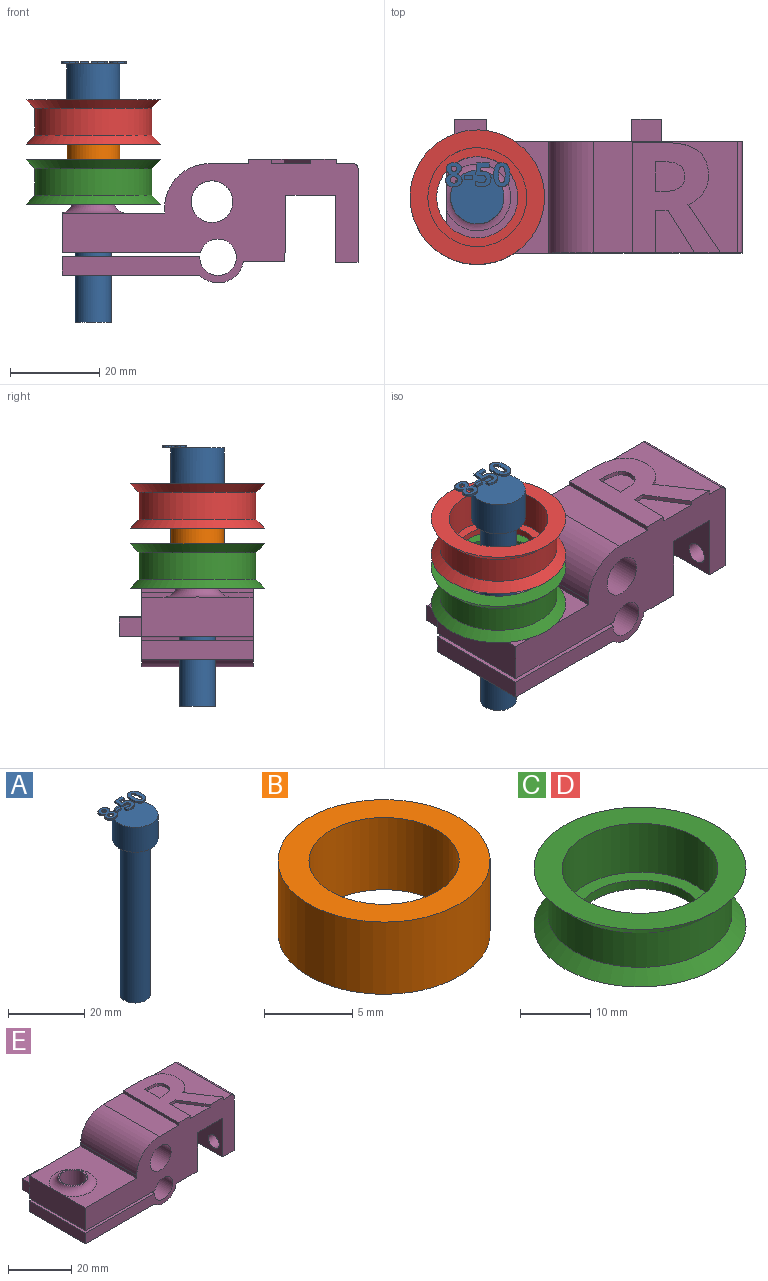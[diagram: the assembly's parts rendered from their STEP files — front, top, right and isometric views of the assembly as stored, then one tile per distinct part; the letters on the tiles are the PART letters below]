
ASSEMBLY  parts=5 mates=4
PART A: 86 faces, bbox 14.5x13.7x58.5 mm
  f0: plane 12x12mm, normal (0,0,1), area 99.4mm2, adj f5,f22,f23,f24,f25,f26,f40,f41
  f1: plane 1x0.26mm, normal (0,0,1), area 0.1mm2, adj f5,f46,f47,f48,f49
  f2: plane 0.85x0.68mm, normal (0,0,1), area 0.2mm2, adj f5,f29,f30,f31
  f3: cylinder r=4mm len=50mm, axis (0,0,-1), area 1256.6mm2, adj f4,f6
  f4: plane 8x8mm, normal (0,0,-1), area 50.3mm2, adj f3
  f5: cylinder r=6mm len=12mm, axis (0,0,-1), area 301.6mm2, adj f0,f1,f2,f6,f39,f45,f67,f85
  f6: plane 12x12mm, normal (0,0,-1), area 62.8mm2, adj f3,f5
  f7: extruded ~0.5x0.46mm, area 0.2mm2, adj f8,f37,f38,f39
  f8: extruded ~0.5x0.46mm, area 0.2mm2, adj f7,f9,f38,f39
  f9: extruded ~0.5x0.39mm, area 0.2mm2, adj f8,f10,f38,f39
  f10: extruded ~0.5x0.4mm, area 0.2mm2, adj f9,f11,f38,f39
  f11: extruded ~0.5x0.49mm, area 0.3mm2, adj f10,f12,f38,f39
  f12: extruded ~0.5x0.5mm, area 0.3mm2, adj f11,f13,f38,f39
  f13: extruded ~0.5x0.39mm, area 0.2mm2, adj f12,f37,f38,f39
  f14: extruded ~1.22x0.5mm, area 0.6mm2, adj f15,f35,f38,f39
  f15: extruded ~1.22x0.5mm, area 0.6mm2, adj f14,f16,f38,f39
  f16: extruded ~0.91x0.5mm, area 0.5mm2, adj f15,f17,f38,f39
  f17: extruded ~0.71x0.5mm, area 0.4mm2, adj f16,f18,f38,f39
  f18: extruded ~0.65x0.61mm, area 0.4mm2, adj f17,f19,f38,f39
  f19: extruded ~0.77x0.62mm, area 0.5mm2, adj f18,f20,f38,f39
  f20: extruded ~0.8x0.5mm, area 0.4mm2, adj f19,f21,f38,f39
  f21: extruded ~1.04x0.5mm, area 0.6mm2, adj f20,f22,f38,f39
  f22: extruded ~1.36x0.5mm, area 0.7mm2, adj f0,f21,f23,f38,f39
  f23: extruded ~1.33x0.5mm, area 0.7mm2, adj f0,f22,f24,f38
  f24: extruded ~1.04x0.51mm, area 0.6mm2, adj f0,f23,f25,f38
  f25: extruded ~0.75x0.5mm, area 0.4mm2, adj f0,f24,f26,f38
  f26: extruded ~0.85x0.66mm, area 0.5mm2, adj f0,f25,f27,f38,f39
  f27: extruded ~0.72x0.56mm, area 0.5mm2, adj f26,f28,f38,f39
  f28: extruded ~0.72x0.5mm, area 0.4mm2, adj f27,f35,f38,f39
  f29: extruded ~0.5x0.45mm, area 0.3mm2, adj f2,f30,f36,f38,f39
  f30: extruded ~0.5x0.47mm, area 0.3mm2, adj f2,f29,f31,f38
  f31: extruded ~0.62x0.5mm, area 0.3mm2, adj f2,f30,f32,f38,f39
  f32: extruded ~0.59x0.5mm, area 0.3mm2, adj f31,f33,f38,f39
  f33: extruded ~0.5x0.48mm, area 0.3mm2, adj f32,f34,f38,f39
  f34: extruded ~0.89x0.77mm, area 0.6mm2, adj f33,f36,f38,f39
  f35: extruded ~0.93x0.5mm, area 0.5mm2, adj f14,f28,f38,f39
  f36: extruded ~0.66x0.5mm, area 0.4mm2, adj f29,f34,f38,f39
  f37: extruded ~0.5x0.39mm, area 0.2mm2, adj f7,f13,f38,f39
  f38: plane 5.4x3.69mm, normal (0,0,1), area 12.7mm2, adj f7,f8,f9,f10,f11,f12,f13,f14
  f39: plane 5.4x3.53mm, normal (0,0,-1), area 10.2mm2, adj f5,f7,f8,f9,f10,f11,f12,f13
  f40: plane 0.9x0.5mm, normal (-1,0,0), area 0.4mm2, adj f0,f41,f43,f44
  f41: plane 1.93x0.5mm, normal (0,-1,0), area 1mm2, adj f0,f40,f42,f44
  f42: plane 0.9x0.5mm, normal (1,0,0), area 0.4mm2, adj f0,f41,f43,f44
  f43: plane 1.93x0.5mm, normal (0,1,0), area 1mm2, adj f0,f40,f42,f44
  f44: plane 1.93x0.9mm, normal (0,0,1), area 1.7mm2, adj f40,f41,f42,f43
  f45: plane 0.76x0.31mm, normal (0,0,-1), area 0mm2, adj f5,f46
  f46: extruded ~1.21x0.5mm, area 0.7mm2, adj f0,f1,f45,f47,f65,f66
  f47: extruded ~0.54x0.5mm, area 0.3mm2, adj f1,f46,f48,f66
  f48: plane 0.5x0.13mm, normal (-0.2,0.98,0), area 0.1mm2, adj f1,f47,f49,f66
  f49: plane 1.03x0.5mm, normal (1,-0.09,0), area 0.5mm2, adj f1,f48,f50,f66,f67
  f50: plane 1.88x0.5mm, normal (0,-1,0), area 0.9mm2, adj f49,f51,f66,f67
  f51: plane 0.94x0.5mm, normal (1,0,0), area 0.5mm2, adj f50,f52,f66,f67
  f52: plane 2.85x0.5mm, normal (0,1,0), area 1.4mm2, adj f51,f53,f66,f67
  f53: plane 2.68x0.5mm, normal (-1,0.07,0), area 1.3mm2, adj f0,f52,f54,f66,f67
  f54: plane 0.5x0.44mm, normal (-0.47,-0.88,0), area 0.3mm2, adj f0,f53,f55,f66
  f55: extruded ~0.5x0.37mm, area 0.2mm2, adj f0,f54,f56,f66
  f56: extruded ~0.5x0.42mm, area 0.2mm2, adj f0,f55,f57,f66
  f57: extruded ~1.05x0.8mm, area 0.8mm2, adj f0,f56,f58,f66
  f58: extruded ~1.02x0.83mm, area 0.8mm2, adj f0,f57,f59,f66
  f59: extruded ~0.72x0.5mm, area 0.4mm2, adj f0,f58,f60,f66
  f60: extruded ~0.66x0.5mm, area 0.4mm2, adj f0,f59,f61,f66
  f61: plane 0.96x0.5mm, normal (-1,0,0), area 0.5mm2, adj f0,f60,f62,f66
  f62: extruded ~1.42x0.5mm, area 0.7mm2, adj f0,f61,f63,f66
  f63: extruded ~1.55x0.5mm, area 0.8mm2, adj f0,f62,f64,f66
  f64: extruded ~1.36x0.54mm, area 0.8mm2, adj f0,f63,f65,f66
  f65: extruded ~1.17x0.5mm, area 0.6mm2, adj f0,f46,f64,f66
  f66: plane 5.33x3.51mm, normal (0,0,1), area 10.9mm2, adj f46,f47,f48,f49,f50,f51,f52,f53
  f67: plane 2.97x1.71mm, normal (0,0,-1), area 3.5mm2, adj f5,f49,f50,f51,f52,f53
  f68: extruded ~1.39x0.5mm, area 0.7mm2, adj f69,f83,f84,f85
  f69: extruded ~1.39x0.5mm, area 0.7mm2, adj f68,f70,f84,f85
  f70: extruded ~0.56x0.5mm, area 0.4mm2, adj f69,f71,f84,f85
  f71: extruded ~0.56x0.5mm, area 0.4mm2, adj f70,f72,f84,f85
  f72: extruded ~1.39x0.5mm, area 0.7mm2, adj f71,f73,f84,f85
  f73: extruded ~1.38x0.5mm, area 0.7mm2, adj f72,f74,f84,f85
  f74: extruded ~0.56x0.5mm, area 0.4mm2, adj f73,f83,f84,f85
  f75: extruded ~2.04x0.5mm, area 1.1mm2, adj f76,f82,f84,f85
  f76: extruded ~2.02x0.5mm, area 1.1mm2, adj f75,f77,f84,f85
  f77: extruded ~1.38x0.69mm, area 0.8mm2, adj f76,f78,f84,f85
  f78: extruded ~1.38x0.66mm, area 0.8mm2, adj f77,f79,f84,f85
  f79: extruded ~2.05x0.5mm, area 1.1mm2, adj f78,f80,f84,f85
  f80: extruded ~2.02x0.5mm, area 1mm2, adj f0,f79,f81,f84,f85
  f81: extruded ~1.37x0.68mm, area 0.8mm2, adj f0,f80,f82,f84
  f82: extruded ~1.39x0.66mm, area 0.8mm2, adj f0,f75,f81,f84,f85
  f83: extruded ~0.56x0.5mm, area 0.4mm2, adj f68,f74,f84,f85
  f84: plane 5.41x3.68mm, normal (0,0,1), area 12.1mm2, adj f68,f69,f70,f71,f72,f73,f74,f75
  f85: plane 5.41x3.68mm, normal (0,0,-1), area 10.3mm2, adj f5,f68,f69,f70,f71,f72,f73,f74
PART B: 4 faces, bbox 12x12x5 mm
  f0: cylinder r=4.25mm len=8.5mm, axis (0,0,-1), area 133.5mm2, adj f2,f3
  f1: cylinder r=6mm len=12mm, axis (0,0,-1), area 188.5mm2, adj f2,f3
  f2: plane 12x12mm, normal (0,0,1), area 56.4mm2, adj f0,f1
  f3: plane 12x12mm, normal (0,0,-1), area 56.4mm2, adj f0,f1
PART C: 8 faces, bbox 30.2x30.2x10 mm
  f0: plane 30.2x30.2mm, normal (0,0,1), area 329.2mm2, adj f1,f7
  f1: cylinder r=11.1mm len=22.2mm, axis (0,0,-1), area 592.8mm2, adj f0,f2
  f2: plane 22.2x22.2mm, normal (0,0,1), area 126.9mm2, adj f1,f3
  f3: cylinder r=9.1mm len=18.2mm, axis (0,0,-1), area 85.8mm2, adj f2,f4
  f4: plane 30.2x30.2mm, normal (0,0,-1), area 456.2mm2, adj f3,f5
  f5: cone r=13.1mm half-angle=45deg, axis (0,0,-1), area 250.6mm2, adj f4,f6
  f6: cylinder r=13.1mm len=26.2mm, axis (0,0,-1), area 493.9mm2, adj f5,f7
  f7: cone r=15.1mm half-angle=45deg, axis (0,0,1), area 250.6mm2, adj f0,f6
PART D: same geometry as C
PART E: 56 faces, bbox 69.9x30x27.7 mm
  f0: plane 32.42x25mm, normal (0,0,1), area 417.1mm2, adj f14,f15,f25,f27,f40,f41,f42,f43
  f1: plane 9.51x8.71mm, normal (0,0,1), area 54.7mm2, adj f14,f37,f38,f39
  f2: plane 25x4.12mm, normal (-1,0,0), area 103mm2, adj f5,f14,f15,f19
  f3: cylinder r=4.17mm len=8.35mm, axis (0,0,1), area 108.1mm2, adj f5,f19
  f4: plane 25x9.34mm, normal (0,0,-1), area 233.4mm2, adj f13,f14,f15,f17
  f5: plane 30.88x25mm, normal (0,0,-1), area 717.2mm2, adj f2,f3,f14,f15,f17
  f6: plane 25x8.82mm, normal (-1,0,0), area 219.6mm2, adj f7,f14,f15,f20,f24
  f7: plane 25x23mm, normal (0,0,1), area 400mm2, adj f6,f8,f14,f15,f24
  f8: plane 25x1.1mm, normal (-1,0,0), area 27.5mm2, adj f7,f14,f15,f25
  f9: plane 25x21.09mm, normal (1,0,0), area 493.5mm2, adj f10,f14,f15,f22,f23,f27
  f10: plane 25x5mm, normal (0,0,-1), area 125mm2, adj f9,f11,f14,f15
  f11: plane 25x15mm, normal (-1,0,0), area 341.3mm2, adj f10,f12,f14,f15,f22,f23
  f12: plane 25x11.2mm, normal (0,0,-1), area 280mm2, adj f11,f13,f14,f15
  f13: plane 25x14.91mm, normal (1,0,-0.01), area 372.8mm2, adj f4,f12,f14,f15
  f14: plane 66.42x27.75mm, normal (0,-1,0), area 1004.9mm2, adj f0,f1,f2,f4,f5,f6,f7,f8
  f15: plane 66.42x26.75mm, normal (0,1,0), area 933.9mm2, adj f0,f2,f4,f5,f6,f7,f8,f9
  f16: cylinder r=4.17mm len=10.78mm, axis (0,0,1), area 282.8mm2, adj f20,f21
  f17: cylinder r=5.75mm len=25mm, axis (0,-1,0), area 315.9mm2, adj f4,f5,f14,f15
  f18: cylinder r=4.1mm len=25mm, axis (0,-1,0), area 618.7mm2, adj f14,f15,f19,f20
  f19: plane 30.91x25mm, normal (0,0,1), area 718.1mm2, adj f2,f3,f14,f15,f18
  f20: plane 31.07x30mm, normal (0,0,-1), area 758.4mm2, adj f6,f14,f15,f16,f18,f29,f30,f31
  f21: plane 9.35x9.35mm, normal (0,0,1), area 13.9mm2, adj f16,f24
  f22: cylinder r=2.43mm len=5mm, axis (1,0,0), area 76.2mm2, adj f9,f11
  f23: cylinder r=2.2mm len=5mm, axis (1,0,0), area 69.1mm2, adj f9,f11
  f24: torus R=7.5mm, axis (0,0,-1), area 134.6mm2, adj f6,f7,f21
  f25: cylinder r=10mm len=25mm, axis (0,-1,0), area 392.7mm2, adj f0,f8,f14,f15
  f26: cylinder r=4.68mm len=25mm, axis (0,-1,0), area 735.2mm2, adj f14,f15
  f27: cylinder r=1mm len=25mm, axis (0,-1,0), area 39.3mm2, adj f0,f9,f14,f15
  f28: plane 7.3x5mm, normal (0,0,1), area 36.5mm2, adj f15,f29,f30,f31
  f29: plane 5x4.12mm, normal (-1,0,0), area 20.6mm2, adj f15,f20,f28,f31
  f30: plane 5x4.12mm, normal (1,0,0), area 20.6mm2, adj f15,f20,f28,f31
  f31: plane 7.3x4.12mm, normal (0,1,0), area 30.1mm2, adj f20,f28,f29,f30
  f32: plane 6.63x5mm, normal (0,0,1), area 33.2mm2, adj f15,f33,f35,f36
  f33: plane 5x4.5mm, normal (-1,0,0), area 22.5mm2, adj f15,f32,f34,f36
  f34: plane 6.63x5mm, normal (0,0,-1), area 33.2mm2, adj f15,f33,f35,f36
  f35: plane 5x4.5mm, normal (1,0,0), area 22.5mm2, adj f15,f32,f34,f36
  f36: plane 6.63x4.5mm, normal (0,1,0), area 29.9mm2, adj f32,f33,f34,f35
  f37: plane 9.51x1mm, normal (1,0,0), area 9.5mm2, adj f1,f14,f38,f54
  f38: plane 2.79x1mm, normal (0,-1,0), area 2.8mm2, adj f1,f37,f39,f54
  f39: plane 9.51x5.92mm, normal (-0.85,-0.53,0), area 11.2mm2, adj f1,f14,f38,f54
  f40: extruded ~10.8x7.29mm, area 13mm2, adj f0,f14,f41,f54
  f41: extruded ~3.41x2.67mm, area 4.4mm2, adj f0,f40,f42,f54
  f42: extruded ~3.89x1.2mm, area 4.1mm2, adj f0,f41,f43,f54
  f43: extruded ~5.59x2.42mm, area 6.3mm2, adj f0,f42,f44,f54
  f44: extruded ~7.48x1.84mm, area 7.8mm2, adj f0,f43,f45,f54
  f45: plane 7.22x1mm, normal (0,1,0), area 7.2mm2, adj f0,f44,f46,f54
  f46: plane 24.79x1mm, normal (-1,0,0), area 24.8mm2, adj f0,f14,f45,f54
  f47: plane 1.69x1mm, normal (0,1,0), area 1.7mm2, adj f48,f53,f54,f55
  f48: plane 6.7x1mm, normal (1,0,0), area 6.7mm2, adj f47,f49,f54,f55
  f49: plane 1.6x1mm, normal (0,-1,0), area 1.6mm2, adj f48,f50,f54,f55
  f50: extruded ~3.75x1mm, area 3.9mm2, adj f49,f51,f54,f55
  f51: extruded ~2.51x1.21mm, area 2.9mm2, adj f50,f52,f54,f55
  f52: extruded ~2.61x1.19mm, area 3mm2, adj f51,f53,f54,f55
  f53: extruded ~3.68x1mm, area 3.8mm2, adj f47,f52,f54,f55
  f54: plane 24.79x19.8mm, normal (0,0,1), area 300mm2, adj f14,f37,f38,f39,f40,f41,f42,f43
  f55: plane 6.7x6.56mm, normal (0,0,1), area 38.8mm2, adj f47,f48,f49,f50,f51,f52,f53
PLACE A t=(-103.78,-12.5,-13.6)mm
PLACE B rot(axis=(1,0,0),180deg) t=(-103.78,-12.5,26.4)mm
PLACE C t=(-103.78,-12.5,18.1)mm
PLACE D t=(-103.78,-12.5,31.6)mm
PLACE E at identity
MATE fastened A.f3 <-> D.f1  axis (0,0,-1) through (-103.78,-12.5,36.4)mm
MATE fastened B.f0 <-> C.f1  axis (0,0,1) through (-103.78,-12.5,21.4)mm
MATE fastened C.f1 <-> E.f3  axis (0,0,-1) through (-103.78,-12.5,12.9)mm
MATE fastened D.f1 <-> B.f0  axis (0,0,-1) through (-103.78,-12.5,26.4)mm
